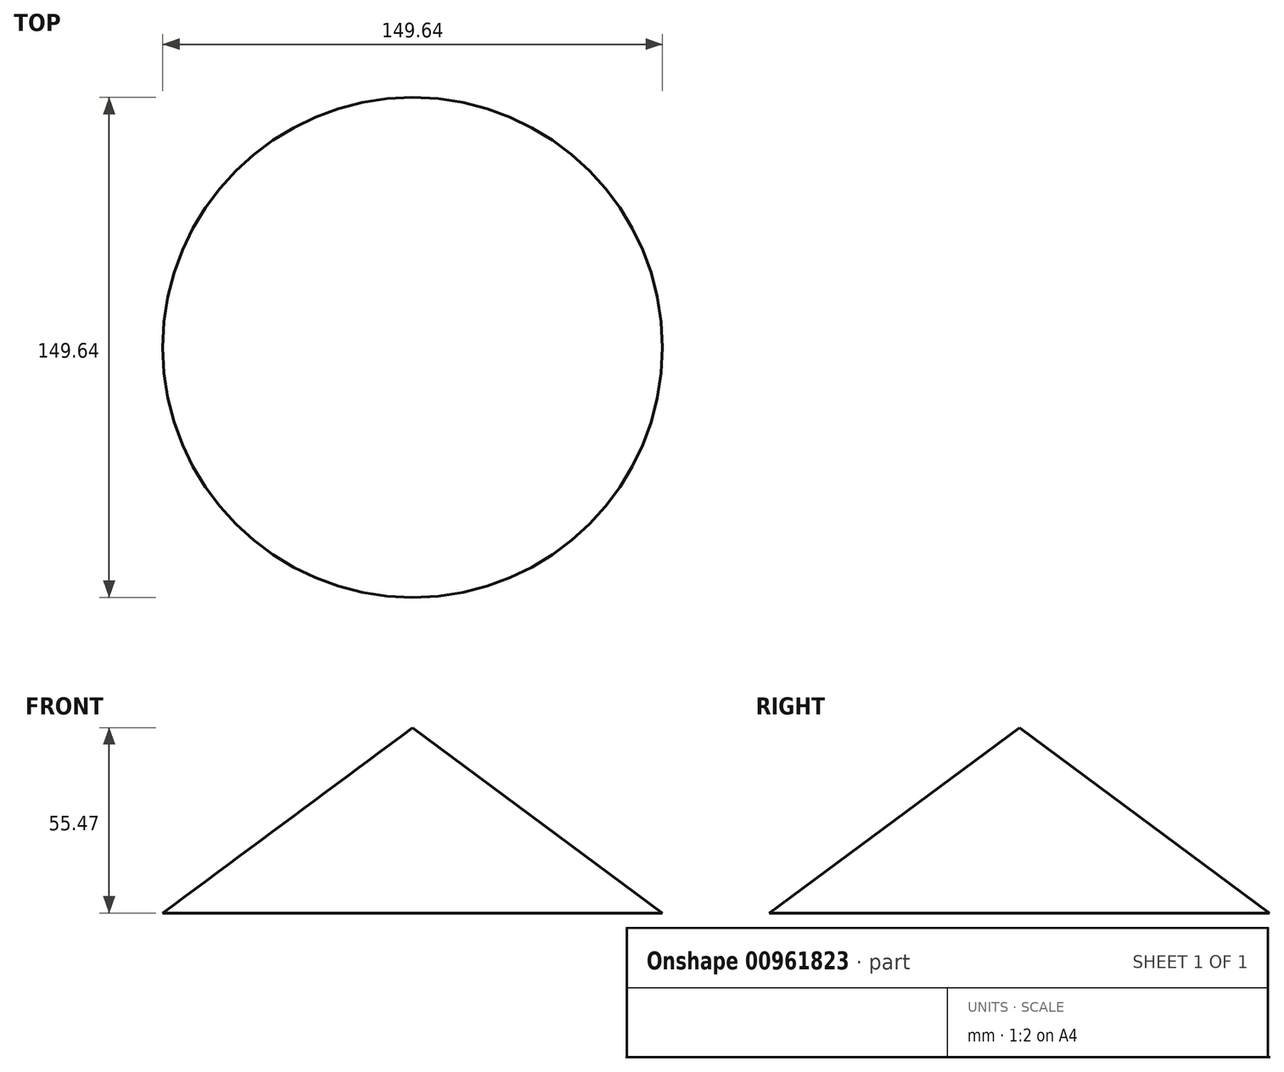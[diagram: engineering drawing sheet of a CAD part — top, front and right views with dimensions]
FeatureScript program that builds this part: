
annotation { "Feature Type Name" : "Feature", "Feature Type Description" : "" }
export const myFeature = defineFeature(function(context is Context, id is Id, definition is map)
    precondition{}
    {
        {
            var Q0;
            Q0=qCreatedBy(makeId("Front.planeOp"),FACE);
            var sketch = newSketch(context, id + "F0", { "sketchPlane" : qUnion([Q0])});
            skLineSegment(sketch, "E0", {"start": v(0, 0) * mm, "end": v(0, 55.47) * mm});
            skLineSegment(sketch, "E1", {"start": v(0, 55.47) * mm, "end": v(74.82, 0) * mm});
            skLineSegment(sketch, "E2", {"start": v(74.82, 0) * mm, "end": v(0, 0) * mm});
            skSolve(sketch);
        }
        {
            var Q0;
            Q0 = qSketchRegion(id + "F0", true);
            var Q1;
            Q1=sQuery(id+"F0.wireOp",EDGE,"E0");
            revolve(context, id + "F1", {"surfaceOperationType" : NewSurfaceOperationType.NEW, "entities" : qUnion([Q0]), "axis" : qUnion([Q1]), "revolveType" : RevolveType.FULL});
        }
    });
